# Revit family: МетеорЛифт_Лифт_Пассажирский_МетеорЛифт_EvoNG_LOD100
name_source: partatom
category: Оборудование
units: mm (PartAtom-declared; Revit-internal decimal feet)

## family parameters
Всегда вертикально = Да
Общий = Да
При загрузке вырезать с полостями = Да
Размер круглого соединителя = Использовать диаметр
Тип детали = Нормальный
Точка расчета площади = Нет

## types (6) — shared parameters
URL = https://meteor.ru
Изготовитель = ООО "Метеор Лифт"
Описание = Лифт электрический пассажирский без машинного помещения
Телефон = 8 800 200 68 47
zero-valued in all types: Отметка по умолчанию

## per-type parameters (varying)
| type | CD | CW | DL | NBPAS | Ось направляющих кабины | Тип кабины | Штихмасс кабины |
| Г/п 450 кг / Кабина 1000х1250 мм (ШхГ) | 1250 мм | 1000 мм | 450 | 6 | 625 мм | 06D | 1080 мм |
| Г/п 630 кг / Кабина 1100х1400 (ШхГ) | 1400 мм | 1100 мм | 630 | 8 | 700 мм | 08D | 1180 мм |
| Г/п 1000 кг / Кабина 1100х2100 (ШхГ) | 2100 мм | 1100 мм | 1000 | 13 | 950 мм | 13D | 1180 мм |
| Г/п 1000 кг / Кабина 1600х1400 (ШхГ) | 1400 мм | 1600 мм | 1000 | 13 | 700 мм | 13W | 1680 мм |
| Г/п 1000 кг / Кабина 2100х1100 (ШхГ) | 1100 мм | 2100 мм | 1000 | 13 | 480 мм | 13X | 2180 мм |
| Г/п 400 кг / Кабина 950х1100 мм (ШхГ) | 1100 мм | 950 мм | 400 | 5 | 550 мм | 06D | 1030 мм |

## geometry (parser evidence)
native form markers: Blend x2, Sweep x1
no freeform markers — native parametric forms only
